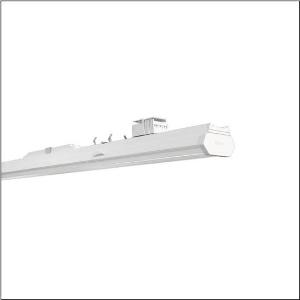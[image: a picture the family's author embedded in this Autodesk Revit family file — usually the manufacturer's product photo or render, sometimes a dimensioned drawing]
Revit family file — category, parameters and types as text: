
# Revit family: licross_r__11_protected_mo_51tp12mn4axg_95e7
name_source: partatom
category: Lighting Fixtures
units: mm (PartAtom-declared; Revit-internal decimal feet)

## family parameters
Cut with Voids When Loaded = No
Host = Face
Light Source = No
Part Type = Normal
Room Calculation Point = No
Round Connector Dimension = Use Diameter
Shared = No

## types (1)
- --- (1 x LED, 10020 lm, 55.3 W, 4000K)
    Apparent Load = 55 VA
    CIE Flux Codes = 73 92 98 99 100
    Color Rendering = 80
    Color Temperature = 4000K
    Default Elevation = 1800 mm
    Description = Licross® 11 Protected MO, luminaire insert, of sheet steel, galvanised, coil coated, white, length: 1.500mm, width: 90mm, height: 101mm, LED rated luminous flux: 10.030lm, light colour: 840, control gear: ON/OFF Multilumen, with plug, 3-pole, with phase selection, mains connection: 220..240V, AC, 50/60Hz, rated input power: 55W, halogen-free wiring, primary light control with lens, of plastic, primary optical cover: cover, of PMMA, light emission: direct distribution, primary light characteristic: symmetric, protection rating (complete): IP64, insulation class (complete): insulation class I (protective earthing), certification: CE, ENEC, VDE, UKCA, protection symbol: D if used in an environment with conductive dust loads with corresponding accessories, impact resistance: IK06, permissible ambient temperature for indoor applications: -35..+40°C, corresponds to IFS (International Featured Standards) requirements for safety and quality in the food industry, reducing of maximum allowable ambient temperature of 5°C with ceiling mounting, LABS conformity tested according to VDMA 24364:2018-05, packaging unit: 1 piece
    Height = 92 mm
    Lamp = 1 x LED
    Lamp Light Flux = 10020 lm
    Lamp Power = 55.3 W
    Lamp count = 1
    Length = 1500 mm
    Luminous efficacy = 181 lm/W
    Manufacturer = Siteco
    ModVariant = No
    Model = 51TP12MN4AXG
    Mounting Place = Ceiling
    Mounting Type = Pendant
    Number of Poles = 1
    OnlyDefault = Yes
    Power Factor = 1
    Product Name = Licross® 11 Protected MO
    Product group = luminaire insert
    ProductGroupID = 901
    Protection Class = Protection class I
    Protection Degree = IP 64
    RLX_Detail_Level = 1
    RLX_Emergency_Light_Flux = 0 lm
    RLX_Emergency_Type = 0
    RLX_Emergency_Type_DB = No
    RlxData = <blob elided: 22053 chars, md5=e4d33fb5>
    Socket = socket
    Standby Power = 0 W
    System Light Flux = 10020 lm
    System Power = 55 W
    Type Comments = factory setting: luminous flux: 100 % | (A | C | E) | 126 mA
    Type Image = l_1256148.jpg
    URL = http://relux.com
    VarID = @adj_055269
    Voltage = 0 V
    Weight = 0.00 kg
    Width = 88 mm

## geometry (parser evidence)
native form markers: Blend x4, Sweep x9
no freeform markers — native parametric forms only
